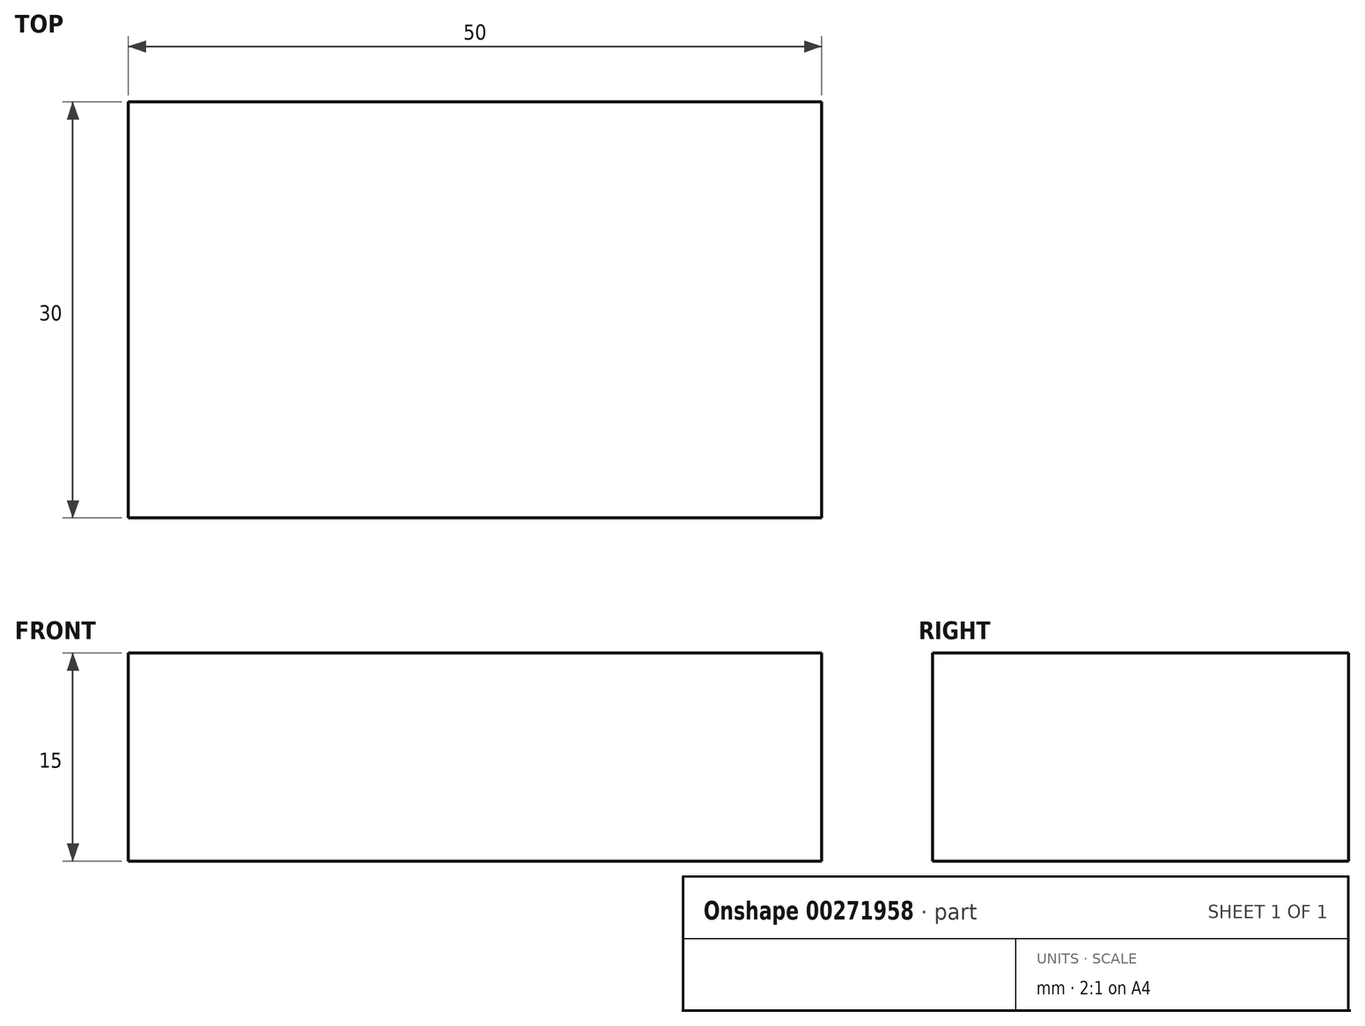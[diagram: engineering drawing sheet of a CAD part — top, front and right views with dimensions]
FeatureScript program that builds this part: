
annotation { "Feature Type Name" : "Feature", "Feature Type Description" : "" }
export const myFeature = defineFeature(function(context is Context, id is Id, definition is map)
    precondition{}
    {
        {
            var Q0;
            Q0=qCreatedBy(makeId("Top.planeOp"),FACE);
            var sketch = newSketch(context, id + "F0", { "sketchPlane" : qUnion([Q0])});
            skLineSegment(sketch, "E0.bottom", {"start": v(0, 0) * mm, "end": v(-50, 0) * mm});
            skLineSegment(sketch, "E0.top", {"start": v(0, 30) * mm, "end": v(-50, 30) * mm});
            skLineSegment(sketch, "E0.left", {"start": v(0, 0) * mm, "end": v(0, 30) * mm});
            skLineSegment(sketch, "E0.right", {"start": v(-50, 0) * mm, "end": v(-50, 30) * mm});
            skSolve(sketch);
        }
        {
            var Q0;
            Q0 = qSketchRegion(id + "F0", true);
            extrude(context, id + "F1", {"entities" : qUnion([Q0]), "depth" : 15 * mm, "offsetDistance" : 25 * mm});
        }
    });
